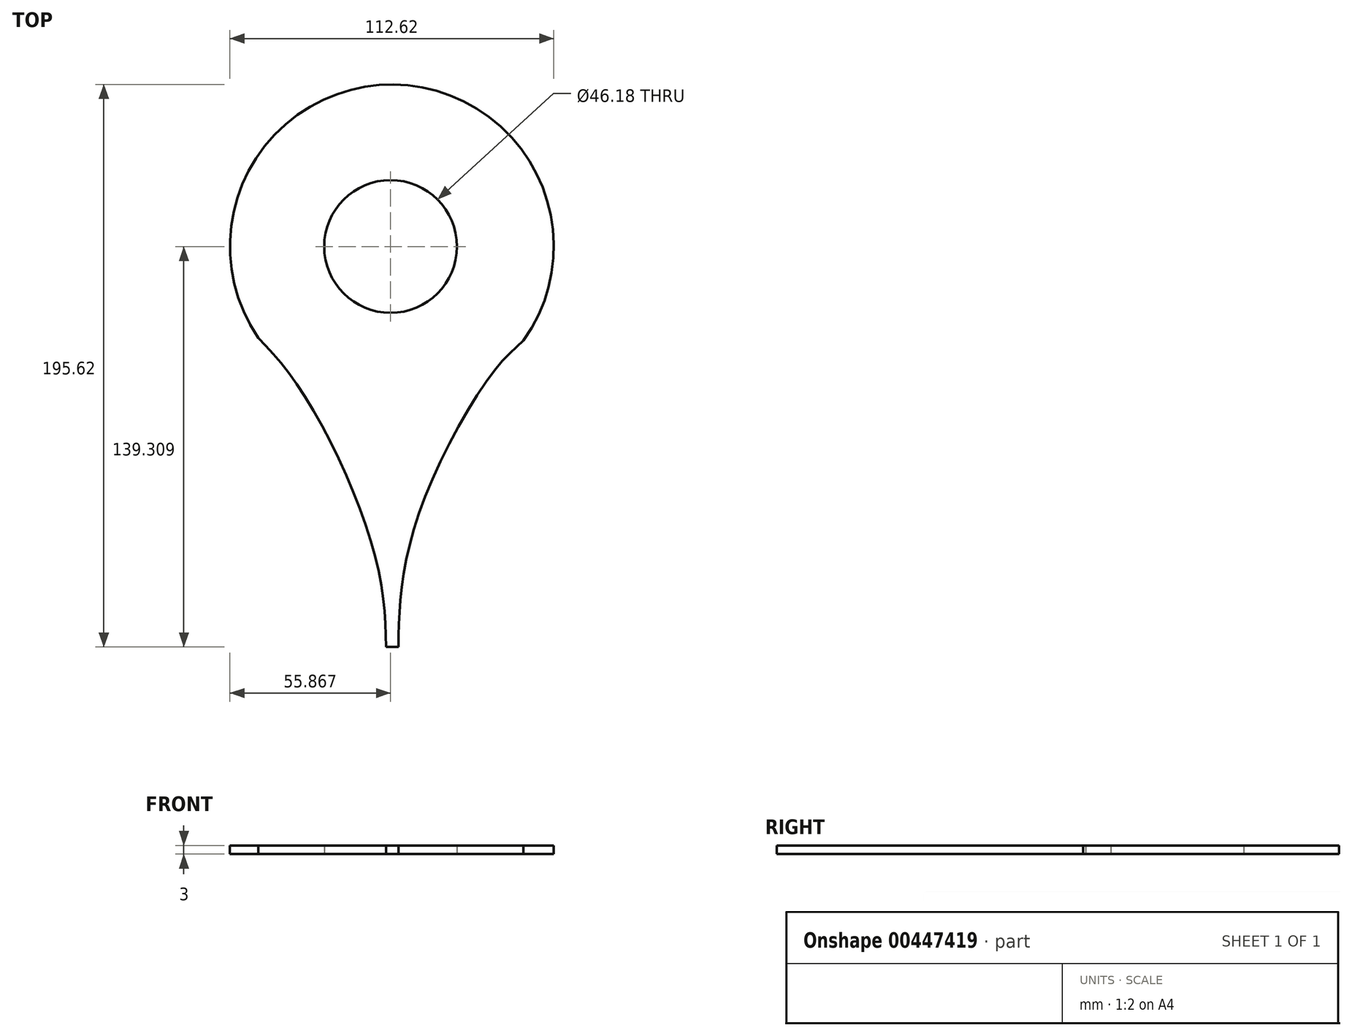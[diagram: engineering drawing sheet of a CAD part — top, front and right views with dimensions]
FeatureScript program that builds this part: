
annotation { "Feature Type Name" : "Feature", "Feature Type Description" : "" }
export const myFeature = defineFeature(function(context is Context, id is Id, definition is map)
    precondition{}
    {
        {
            var Q0;
            Q0=qCreatedBy(makeId("Top.planeOp"),FACE);
            var sketch = newSketch(context, id + "F0", { "sketchPlane" : qUnion([Q0])});
            skCircle(sketch, "E0", {"center": v(-15.91, 53.5) * mm, "radius": 23.09 * mm});
            skPoint(sketch, "E0.first.point", {"position": v(-33.82, 68.09) * mm});
            skPoint(sketch, "E0.second.point", {"position": v(6.07, 60.56) * mm});
            skPoint(sketch, "E0.third.point", {"position": v(-14.4, 30.47) * mm});
            skSolve(sketch);
        }
        {
            var Q0;
            Q0=qCreatedBy(makeId("Top.planeOp"),FACE);
            var sketch = newSketch(context, id + "F1", { "sketchPlane" : qUnion([Q0])});
            skArc(sketch, "E1", {"start": v(24.44, 13.77) * mm, "mid": v(-14.44, 109.8) * mm, "end": v(-56.8, 15.26) * mm});
            skPoint(sketch, "E1.first.point", {"position": v(-61.18, 86.39) * mm});
            skPoint(sketch, "E1.second.point", {"position": v(6.74, 105.25) * mm});
            skPoint(sketch, "E1.third.point", {"position": v(40.25, 61.65) * mm});
            skFitSpline(sketch, "E2", {"points": [v(-13.17, -85.8) * mm, v(0, -30.44) * mm, v(30.34, 20.75) * mm], "startDerivative": vector(6.32, 122.94) * mm, "endDerivative": vector(65.3, 68.34) * mm});
            skFitSpline(sketch, "E3", {"points": [v(-17.45, -85.75) * mm, v(-31.97, -29.34) * mm, v(-61.95, 21.71) * mm], "startDerivative": vector(-9.54, 126.56) * mm, "endDerivative": vector(-75.08, 88.5) * mm});
            skLineSegment(sketch, "E4", {"start": v(-17.45, -85.75) * mm, "end": v(-13.17, -85.8) * mm});
            skSolve(sketch);
        }
        {
            var Q0;
            Q0=makeQuery(id+"F0.imprint","IMPRINT",FACE,{"disambiguationData":[TD([[makeQuery(id+"F0.imprint","IMPRINT",EDGE,{"derivedFrom":sQuery(id+"F0.wireOp",EDGE,"E0")}),1.0]])]});
            var sketch = newSketch(context, id + "F2", { "sketchPlane" : qUnion([Q0])});
            skCircle(sketch, "E5.0", {"center": v(-15.91, 53.5) * mm, "radius": 23.09 * mm});
            skArc(sketch, "E6.0", {"start": v(24.44, 13.77) * mm, "mid": v(-14.44, 109.8) * mm, "end": v(-56.8, 15.26) * mm});
            skFitSpline(sketch, "E7.0", {"points": [v(-17.45, -85.75) * mm, v(-19.04, -64.74) * mm, v(-29.85, -29.46) * mm, v(-49.39, 6.9) * mm, v(-61.95, 21.71) * mm]});
            skFitSpline(sketch, "E8.0", {"points": [v(-13.17, -85.8) * mm, v(-12.12, -65.54) * mm, v(-3.25, -31.9) * mm, v(19.33, 9.23) * mm, v(30.34, 20.75) * mm]});
            skPoint(sketch, "E9.0", {"position": v(-15.31, -85.77) * mm});
            skLineSegment(sketch, "E10.0", {"start": v(-17.45, -85.75) * mm, "end": v(-13.17, -85.8) * mm});
            skSolve(sketch);
        }
        {
            var Q0;
            Q0 = qSketchRegion(id + "F2", true);
            extrude(context, id + "F3", {"entities" : qUnion([Q0]), "depth" : 3 * mm});
        }
        {
            var Q0;
            Q0 = qSketchRegion(id + "F0", true);
            extrude(context, id + "F4", {"entities" : qUnion([Q0]), "depth" : 3 * mm});
        }
    });
